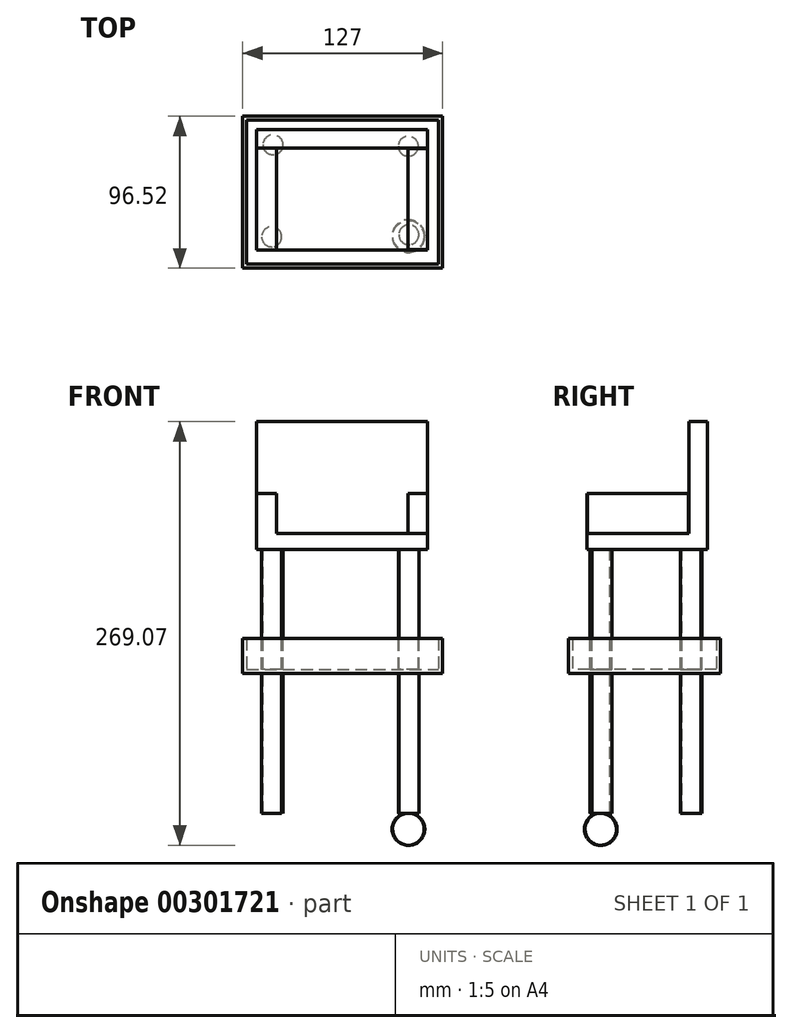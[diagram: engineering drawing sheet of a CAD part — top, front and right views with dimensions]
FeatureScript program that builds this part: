
annotation { "Feature Type Name" : "Feature", "Feature Type Description" : "" }
export const myFeature = defineFeature(function(context is Context, id is Id, definition is map)
    precondition{}
    {
        {
            var Q0;
            Q0=qCreatedBy(makeId("Top.planeOp"),FACE);
            var sketch = newSketch(context, id + "F0", { "sketchPlane" : qUnion([Q0])});
            skLineSegment(sketch, "E0.bottom", {"start": v(-59.16, 46.43) * mm, "end": v(67.84, 46.43) * mm});
            skLineSegment(sketch, "E0.top", {"start": v(-59.16, -50.1) * mm, "end": v(67.84, -50.1) * mm});
            skLineSegment(sketch, "E0.left", {"start": v(-59.16, 46.43) * mm, "end": v(-59.16, -50.1) * mm});
            skLineSegment(sketch, "E0.right", {"start": v(67.84, 46.43) * mm, "end": v(67.84, -50.1) * mm});
            skSolve(sketch);
        }
        {
            var Q0;
            Q0=makeQuery(id+"F0.imprint","IMPRINT",FACE,{"disambiguationData":[TD([[makeQuery(id+"F0.imprint","IMPRINT",EDGE,{"derivedFrom":sQuery(id+"F0.wireOp",EDGE,"E0.bottom")}),-1.0]])]});
            extrude(context, id + "F1", {"entities" : qUnion([Q0]), "depth" : 20.57 * mm});
        }
        {
            var Q0;
            Q0=makeQuery(id+"F1.opExtrude","CAP_FACE",FACE,{"disambiguationData":[OSD([sQuery(id+"F0.wireOp",EDGE,"E0.bottom"),sQuery(id+"F0.wireOp",EDGE,"E0.top"),sQuery(id+"F0.wireOp",EDGE,"E0.left"),sQuery(id+"F0.wireOp",EDGE,"E0.right")])],"isStart":false});
            shell(context, id + "F2", {"entities" : qUnion([Q0]), "thickness" : 2.54 * mm});
        }
        {
            var Q0;
            Q0=makeQuery(id+"F1.opExtrude","CAP_FACE",FACE,{"disambiguationData":[OSD([sQuery(id+"F0.wireOp",EDGE,"E0.bottom"),sQuery(id+"F0.wireOp",EDGE,"E0.top"),sQuery(id+"F0.wireOp",EDGE,"E0.left"),sQuery(id+"F0.wireOp",EDGE,"E0.right")])],"isStart":true});
            var sketch = newSketch(context, id + "F3", { "sketchPlane" : qUnion([Q0])});
            skCircle(sketch, "E1", {"center": v(-40.84, 30.18) * mm, "radius": 6.35 * mm});
            skCircle(sketch, "E2", {"center": v(-39.95, -28.29) * mm, "radius": 6.35 * mm});
            skCircle(sketch, "E3", {"center": v(45.97, -27.4) * mm, "radius": 6.35 * mm});
            skCircle(sketch, "E4", {"center": v(46.39, 28.85) * mm, "radius": 6.35 * mm});
            skSolve(sketch);
        }
        {
            var Q0;
            Q0=makeQuery(id+"F0.imprint","IMPRINT",FACE,{"disambiguationData":[TD([[makeQuery(id+"F0.imprint","IMPRINT",EDGE,{"derivedFrom":sQuery(id+"F0.wireOp",EDGE,"E0.bottom")}),-1.0]])]});
            extrude(context, id + "F4", {"entities" : qUnion([Q0]), "depth" : 22.1 * mm});
        }
        {
            var Q0;
            Q0=makeQuery(id+"F4.opExtrude","CAP_FACE",FACE,{"disambiguationData":[OSD([sQuery(id+"F0.wireOp",EDGE,"E0.bottom"),sQuery(id+"F0.wireOp",EDGE,"E0.top"),sQuery(id+"F0.wireOp",EDGE,"E0.left"),sQuery(id+"F0.wireOp",EDGE,"E0.right")])],"isStart":false});
            shell(context, id + "F5", {"entities" : qUnion([Q0]), "thickness" : 2.54 * mm});
        }
        {
            var Q0;
            Q0=makeQuery(id+"F3.imprint","IMPRINT",FACE,{"disambiguationData":[TD([[makeQuery(id+"F3.imprint","IMPRINT",EDGE,{"derivedFrom":sQuery(id+"F3.wireOp",EDGE,"E4")}),1.0]])]});
            extrude(context, id + "F6", {"entities" : qUnion([Q0]), "operationType" : NewBodyOperationType.ADD, "endBound" : BoundingType.SYMMETRIC, "depth" : 177.8 * mm});
        }
        {
            var Q0;
            Q0=makeQuery(id+"F3.imprint","IMPRINT",FACE,{"disambiguationData":[TD([[makeQuery(id+"F3.imprint","IMPRINT",EDGE,{"derivedFrom":sQuery(id+"F3.wireOp",EDGE,"E1")}),1.0]])]});
            var Q1;
            Q1=makeQuery(id+"F3.imprint","IMPRINT",FACE,{"disambiguationData":[TD([[makeQuery(id+"F3.imprint","IMPRINT",EDGE,{"derivedFrom":sQuery(id+"F3.wireOp",EDGE,"E3")}),1.0]])]});
            var Q2;
            Q2=makeQuery(id+"F3.imprint","IMPRINT",FACE,{"disambiguationData":[TD([[makeQuery(id+"F3.imprint","IMPRINT",EDGE,{"derivedFrom":sQuery(id+"F3.wireOp",EDGE,"E2")}),1.0]])]});
            extrude(context, id + "F7", {"entities" : qUnion([Q0, Q1, Q2]), "operationType" : NewBodyOperationType.ADD, "endBound" : BoundingType.SYMMETRIC, "depth" : 177.8 * mm});
        }
        {
            var Q0;
            Q0=makeQuery(id+"F7.opExtrude","CAP_FACE",FACE,{"disambiguationData":[OSD([sQuery(id+"F3.wireOp",EDGE,"E2")])],"isStart":true});
            var sketch = newSketch(context, id + "F8", { "sketchPlane" : qUnion([Q0])});
            skLineSegment(sketch, "E5.bottom", {"start": v(-50.45, 38.04) * mm, "end": v(58.29, 38.04) * mm});
            skLineSegment(sketch, "E5.top", {"start": v(-50.45, -38.45) * mm, "end": v(58.29, -38.45) * mm});
            skLineSegment(sketch, "E5.left", {"start": v(-50.45, 38.04) * mm, "end": v(-50.45, -38.45) * mm});
            skLineSegment(sketch, "E5.right", {"start": v(58.29, 38.04) * mm, "end": v(58.29, -38.45) * mm});
            skSolve(sketch);
        }
        {
            var Q0;
            Q0=makeQuery(id+"F8.imprint","IMPRINT",FACE,{"disambiguationData":[TD([[makeQuery(id+"F8.imprint","IMPRINT",EDGE,{"derivedFrom":sQuery(id+"F8.wireOp",EDGE,"E5.bottom")}),-1.0]])]});
            extrude(context, id + "F9", {"entities" : qUnion([Q0]), "operationType" : NewBodyOperationType.ADD, "oppositeDirection" : true, "depth" : 10.4 * mm});
        }
        {
            var Q0;
            {var subQ0=sQuery(id+"F3.wireOp",EDGE,"E2");Q0=makeQuery(id+"F9.boolean.opBoolean","MERGE",FACE,{"derivedFrom":[makeQuery(id+"F6.opExtrude","CAP_FACE",FACE,{"disambiguationData":[OSD([sQuery(id+"F3.wireOp",EDGE,"E4")])],"isStart":true}),makeQuery(id+"F7.opExtrude","CAP_FACE",FACE,{"disambiguationData":[OSD([sQuery(id+"F3.wireOp",EDGE,"E1")])],"isStart":true}),makeQuery(id+"F7.opExtrude","CAP_FACE",FACE,{"disambiguationData":[OSD([subQ0])],"isStart":true}),makeQuery(id+"F7.opExtrude","CAP_FACE",FACE,{"disambiguationData":[OSD([sQuery(id+"F3.wireOp",EDGE,"E3")])],"isStart":true}),makeQuery(id+"F9.opExtrude","CAP_FACE",FACE,{"disambiguationData":[OSD([subQ0,sQuery(id+"F8.wireOp",EDGE,"E5.bottom"),sQuery(id+"F8.wireOp",EDGE,"E5.top"),sQuery(id+"F8.wireOp",EDGE,"E5.left"),sQuery(id+"F8.wireOp",EDGE,"E5.right")])],"isStart":true})]});}
            var sketch = newSketch(context, id + "F10", { "sketchPlane" : qUnion([Q0])});
            skLineSegment(sketch, "E6.bottom", {"start": v(-50.45, 38.04) * mm, "end": v(58.29, 38.04) * mm});
            skLineSegment(sketch, "E6.top", {"start": v(-50.45, 26.18) * mm, "end": v(58.29, 26.18) * mm});
            skLineSegment(sketch, "E6.left", {"start": v(-50.45, 38.04) * mm, "end": v(-50.45, 26.18) * mm});
            skLineSegment(sketch, "E6.right", {"start": v(58.29, 38.04) * mm, "end": v(58.29, 26.18) * mm});
            skSolve(sketch);
        }
        {
            var Q0;
            Q0=makeQuery(id+"F10.imprint","IMPRINT",FACE,{"disambiguationData":[TD([[makeQuery(id+"F10.imprint","IMPRINT",EDGE,{"derivedFrom":sQuery(id+"F10.wireOp",EDGE,"E6.bottom")}),-1.0]])]});
            extrude(context, id + "F11", {"entities" : qUnion([Q0]), "operationType" : NewBodyOperationType.ADD, "depth" : 70.87 * mm});
        }
        {
            var Q0;
            {var subQ0=sQuery(id+"F3.wireOp",EDGE,"E2");Q0=makeQuery(id+"F9.boolean.opBoolean","MERGE",FACE,{"derivedFrom":[makeQuery(id+"F6.opExtrude","CAP_FACE",FACE,{"disambiguationData":[OSD([sQuery(id+"F3.wireOp",EDGE,"E4")])],"isStart":true}),makeQuery(id+"F7.opExtrude","CAP_FACE",FACE,{"disambiguationData":[OSD([sQuery(id+"F3.wireOp",EDGE,"E1")])],"isStart":true}),makeQuery(id+"F7.opExtrude","CAP_FACE",FACE,{"disambiguationData":[OSD([subQ0])],"isStart":true}),makeQuery(id+"F7.opExtrude","CAP_FACE",FACE,{"disambiguationData":[OSD([sQuery(id+"F3.wireOp",EDGE,"E3")])],"isStart":true}),makeQuery(id+"F9.opExtrude","CAP_FACE",FACE,{"disambiguationData":[OSD([subQ0,sQuery(id+"F8.wireOp",EDGE,"E5.bottom"),sQuery(id+"F8.wireOp",EDGE,"E5.top"),sQuery(id+"F8.wireOp",EDGE,"E5.left"),sQuery(id+"F8.wireOp",EDGE,"E5.right")])],"isStart":true})]});}
            var sketch = newSketch(context, id + "F12", { "sketchPlane" : qUnion([Q0])});
            skLineSegment(sketch, "E7.bottom", {"start": v(-50.45, -38.45) * mm, "end": v(-37.75, -38.45) * mm});
            skLineSegment(sketch, "E7.top", {"start": v(-50.45, 26.18) * mm, "end": v(-37.75, 26.18) * mm});
            skLineSegment(sketch, "E7.left", {"start": v(-50.45, -38.45) * mm, "end": v(-50.45, 26.18) * mm});
            skLineSegment(sketch, "E7.right", {"start": v(-37.75, -38.45) * mm, "end": v(-37.75, 26.18) * mm});
            skSolve(sketch);
        }
        {
            var Q0;
            {var subQ0=sQuery(id+"F12.wireOp",EDGE,"E7.right");Q0=makeQuery(id+"F12.imprint","IMPRINT",FACE,{"disambiguationData":[TD([[makeQuery(id+"F12.imprint","IMPRINT",EDGE,{"derivedFrom":subQ0}),-1.0]])]});}
            var sketch = newSketch(context, id + "F13", { "sketchPlane" : qUnion([Q0])});
            skSolve(sketch);
        }
        {
            var Q0;
            Q0=makeQuery(id+"F12.imprint","IMPRINT",FACE,{"disambiguationData":[TD([[makeQuery(id+"F12.imprint","IMPRINT",EDGE,{"derivedFrom":sQuery(id+"F12.wireOp",EDGE,"E7.bottom")}),1.0]])]});
            extrude(context, id + "F14", {"entities" : qUnion([Q0]), "operationType" : NewBodyOperationType.ADD, "depth" : 25.4 * mm});
        }
        {
            var Q0;
            {var subQ0=sQuery(id+"F12.wireOp",EDGE,"E7.right");Q0=makeQuery(id+"F13.imprint","IMPRINT",FACE,{"disambiguationData":[TD([[makeQuery(id+"F13.imprint","IMPRINT",EDGE,{"derivedFrom":makeQuery(id+"F12.imprint","IMPRINT",EDGE,{"derivedFrom":subQ0})}),-1.0]])]});}
            var sketch = newSketch(context, id + "F15", { "sketchPlane" : qUnion([Q0])});
            skLineSegment(sketch, "E8.bottom", {"start": v(58.06, -38.2) * mm, "end": v(45.82, -38.2) * mm});
            skLineSegment(sketch, "E8.top", {"start": v(58.06, 25.92) * mm, "end": v(45.82, 25.92) * mm});
            skLineSegment(sketch, "E8.left", {"start": v(58.06, -38.2) * mm, "end": v(58.06, 25.92) * mm});
            skLineSegment(sketch, "E8.right", {"start": v(45.82, -38.2) * mm, "end": v(45.82, 25.92) * mm});
            skSolve(sketch);
        }
        {
            var Q0;
            Q0=makeQuery(id+"F15.imprint","IMPRINT",FACE,{"disambiguationData":[TD([[makeQuery(id+"F15.imprint","IMPRINT",EDGE,{"derivedFrom":sQuery(id+"F15.wireOp",EDGE,"E8.bottom")}),-1.0]])]});
            extrude(context, id + "F16", {"entities" : qUnion([Q0]), "operationType" : NewBodyOperationType.ADD, "depth" : 25.4 * mm});
        }
        {
            var Q0;
            Q0=qCreatedBy(makeId("Front.planeOp"),FACE);
            cPlane(context, id + "F17", {"entities" : qUnion([Q0]), "cplaneType" : CPlaneType.OFFSET, "offset" : 29.72 * mm, "width" : 152.4 * mm, "height" : 152.4 * mm});
        }
        {
            var Q0;
            Q0=qCreatedBy(id+"F17.planeOp",FACE);
            var sketch = newSketch(context, id + "F18", { "sketchPlane" : qUnion([Q0])});
            skLineSegment(sketch, "E9", {"start": v(46.03, -88.9) * mm, "end": v(46.03, -129.7) * mm, "construction": true});
            skLineSegment(sketch, "E10", {"start": v(46.03, -109.3) * mm, "end": v(46.03, -88.9) * mm});
            skArc(sketch, "E11", {"start": v(46.03, -88.9) * mm, "mid": v(36.03, -99.1) * mm, "end": v(46.03, -109.3) * mm});
            skSolve(sketch);
        }
        {
            var Q0;
            Q0=makeQuery(id+"F18.imprint","IMPRINT",FACE,{"disambiguationData":[TD([[makeQuery(id+"F18.imprint","IMPRINT",EDGE,{"derivedFrom":sQuery(id+"F18.wireOp",EDGE,"E10")}),1.0]])]});
            var Q1;
            Q1=sQuery(id+"F18.wireOp",EDGE,"E10");
            revolve(context, id + "F19", {"entities" : qUnion([Q0]), "axis" : qUnion([Q1]), "revolveType" : RevolveType.FULL});
        }
    });
